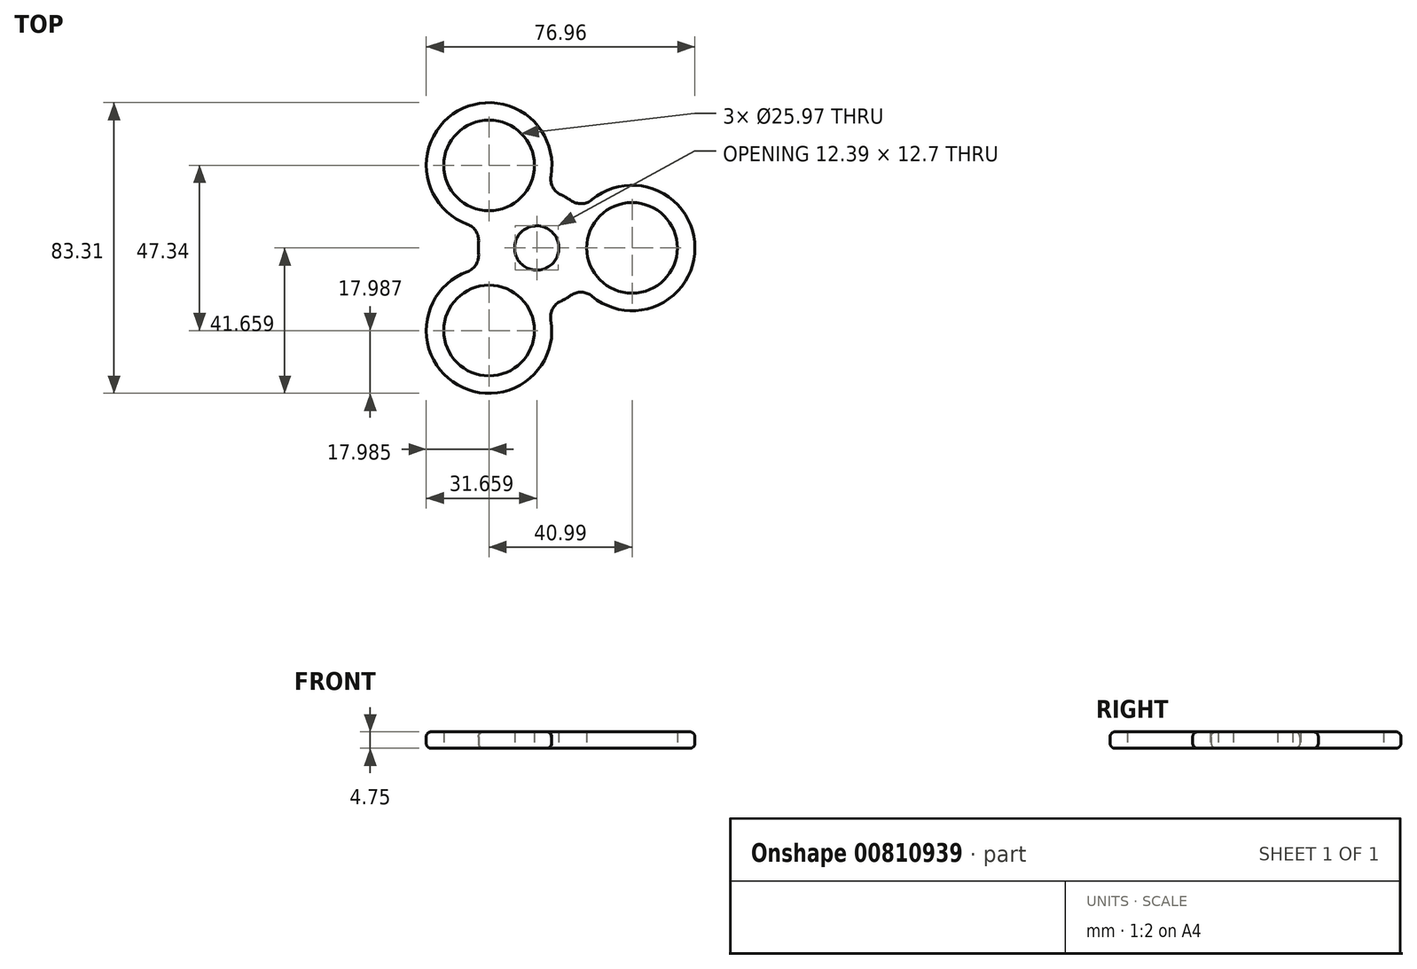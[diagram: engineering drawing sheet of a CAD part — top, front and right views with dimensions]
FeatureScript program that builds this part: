
annotation { "Feature Type Name" : "Feature", "Feature Type Description" : "" }
export const myFeature = defineFeature(function(context is Context, id is Id, definition is map)
    precondition{}
    {
        {
            var Q0;
            Q0=qCreatedBy(makeId("Top.planeOp"),FACE);
            var sketch = newSketch(context, id + "F0", { "sketchPlane" : qUnion([Q0])});
            skCircle(sketch, "E0", {"center": v(0, 0) * mm, "radius": 6.34 * mm});
            skCircle(sketch, "E1.1.4", {"center": v(0, 0.02) * mm, "radius": 6.33 * mm});
            skCircle(sketch, "E2", {"center": v(-13.68, -23.66) * mm, "radius": 12.98 * mm});
            skCircle(sketch, "E3", {"center": v(27.31, 0.02) * mm, "radius": 12.98 * mm});
            skCircle(sketch, "E4", {"center": v(-13.66, 23.68) * mm, "radius": 12.98 * mm});
            skArc(sketch, "E5.0", {"start": v(6.91, -15.23) * mm, "mid": v(8.36, -14.48) * mm, "end": v(9.73, -13.6) * mm});
            skArc(sketch, "E6.0", {"start": v(15.83, -13.82) * mm, "mid": v(45.3, 0.02) * mm, "end": v(15.83, 13.86) * mm});
            skArc(sketch, "E7.0", {"start": v(-19.9, -6.8) * mm, "mid": v(-22.67, -39.24) * mm, "end": v(4.05, -20.62) * mm});
            skArc(sketch, "E8.0", {"start": v(4.07, 20.65) * mm, "mid": v(-22.65, 39.25) * mm, "end": v(-19.9, 6.81) * mm});
            skArc(sketch, "E9.trimOffspring", {"start": v(9.73, 13.64) * mm, "mid": v(8.37, 14.52) * mm, "end": v(6.93, 15.26) * mm});
            skArc(sketch, "E10.trimOffspring", {"start": v(-16.66, 1.64) * mm, "mid": v(-16.74, 0.01) * mm, "end": v(-16.66, -1.61) * mm});
            skPoint(sketch, "E11.visualSharp", {"position": v(2.84, 16.52) * mm});
            skArc(sketch, "E11.filletArc", {"start": v(4.07, 20.65) * mm, "mid": v(4.58, 17.47) * mm, "end": v(6.93, 15.26) * mm});
            skPoint(sketch, "E12.visualSharp", {"position": v(12.87, 10.73) * mm});
            skArc(sketch, "E12.filletArc", {"start": v(9.73, 13.64) * mm, "mid": v(12.82, 12.71) * mm, "end": v(15.83, 13.86) * mm});
            skPoint(sketch, "E13.visualSharp", {"position": v(-15.7, -5.8) * mm});
            skArc(sketch, "E13.filletArc", {"start": v(-19.9, -6.8) * mm, "mid": v(-17.4, -4.76) * mm, "end": v(-16.66, -1.61) * mm});
            skPoint(sketch, "E14.visualSharp", {"position": v(-15.7, 5.8) * mm});
            skArc(sketch, "E14.filletArc", {"start": v(-16.66, 1.64) * mm, "mid": v(-17.4, 4.78) * mm, "end": v(-19.9, 6.81) * mm});
            skPoint(sketch, "E15.visualSharp", {"position": v(2.81, -16.48) * mm});
            skArc(sketch, "E15.filletArc", {"start": v(6.91, -15.23) * mm, "mid": v(4.56, -17.44) * mm, "end": v(4.05, -20.62) * mm});
            skPoint(sketch, "E16.visualSharp", {"position": v(12.87, -10.69) * mm});
            skArc(sketch, "E16.filletArc", {"start": v(15.83, -13.82) * mm, "mid": v(12.82, -12.67) * mm, "end": v(9.73, -13.6) * mm});
            skSolve(sketch);
        }
        {
            var Q0;
            Q0=makeQuery(id+"F0.imprint","IMPRINT",FACE,{"disambiguationData":[TD([[makeQuery(id+"F0.imprint","IMPRINT",EDGE,{"derivedFrom":sQuery(id+"F0.wireOp",EDGE,"E2")}),-1.0]])]});
            extrude(context, id + "F1", {"entities" : qUnion([Q0]), "depth" : 4.75 * mm, "offsetDistance" : 25 * mm});
        }
        {
            var Q0;
            Q0=makeQuery(id+"F1.opExtrude","CAP_EDGE",EDGE,{"disambiguationData":[OSD([sQuery(id+"F0.wireOp",EDGE,"E7.0")])],"isStart":false});
            var Q1;
            Q1=makeQuery(id+"F1.opExtrude","CAP_EDGE",EDGE,{"disambiguationData":[OSD([sQuery(id+"F0.wireOp",EDGE,"E6.0")])],"isStart":true});
            var Q2;
            Q2=makeQuery(id+"F1.opExtrude","CAP_EDGE",EDGE,{"disambiguationData":[OSD([sQuery(id+"F0.wireOp",EDGE,"E13.filletArc")])],"isStart":true});
            var Q3;
            Q3=makeQuery(id+"F1.opExtrude","CAP_EDGE",EDGE,{"disambiguationData":[OSD([sQuery(id+"F0.wireOp",EDGE,"E7.0")])],"isStart":true});
            var Q4;
            Q4=makeQuery(id+"F1.opExtrude","CAP_EDGE",EDGE,{"disambiguationData":[OSD([sQuery(id+"F0.wireOp",EDGE,"E10.trimOffspring")])],"isStart":true});
            var Q5;
            Q5=makeQuery(id+"F1.opExtrude","CAP_EDGE",EDGE,{"disambiguationData":[OSD([sQuery(id+"F0.wireOp",EDGE,"E14.filletArc")])],"isStart":true});
            var Q6;
            Q6=makeQuery(id+"F1.opExtrude","CAP_EDGE",EDGE,{"disambiguationData":[OSD([sQuery(id+"F0.wireOp",EDGE,"E8.0")])],"isStart":true});
            var Q7;
            Q7=makeQuery(id+"F1.opExtrude","CAP_EDGE",EDGE,{"disambiguationData":[OSD([sQuery(id+"F0.wireOp",EDGE,"E15.filletArc")])],"isStart":false});
            var Q8;
            Q8=makeQuery(id+"F1.opExtrude","CAP_EDGE",EDGE,{"disambiguationData":[OSD([sQuery(id+"F0.wireOp",EDGE,"E5.0")])],"isStart":false});
            var Q9;
            Q9=makeQuery(id+"F1.opExtrude","CAP_EDGE",EDGE,{"disambiguationData":[OSD([sQuery(id+"F0.wireOp",EDGE,"E16.filletArc")])],"isStart":false});
            var Q10;
            Q10=makeQuery(id+"F1.opExtrude","CAP_EDGE",EDGE,{"disambiguationData":[OSD([sQuery(id+"F0.wireOp",EDGE,"E16.filletArc")])],"isStart":true});
            var Q11;
            Q11=makeQuery(id+"F1.opExtrude","CAP_EDGE",EDGE,{"disambiguationData":[OSD([sQuery(id+"F0.wireOp",EDGE,"E5.0")])],"isStart":true});
            var Q12;
            Q12=makeQuery(id+"F1.opExtrude","CAP_EDGE",EDGE,{"disambiguationData":[OSD([sQuery(id+"F0.wireOp",EDGE,"E15.filletArc")])],"isStart":true});
            var Q13;
            Q13=makeQuery(id+"F1.opExtrude","CAP_EDGE",EDGE,{"disambiguationData":[OSD([sQuery(id+"F0.wireOp",EDGE,"E6.0")])],"isStart":false});
            var Q14;
            Q14=makeQuery(id+"F1.opExtrude","CAP_EDGE",EDGE,{"disambiguationData":[OSD([sQuery(id+"F0.wireOp",EDGE,"E12.filletArc")])],"isStart":false});
            var Q15;
            Q15=makeQuery(id+"F1.opExtrude","CAP_EDGE",EDGE,{"disambiguationData":[OSD([sQuery(id+"F0.wireOp",EDGE,"E9.trimOffspring")])],"isStart":false});
            var Q16;
            Q16=makeQuery(id+"F1.opExtrude","CAP_EDGE",EDGE,{"disambiguationData":[OSD([sQuery(id+"F0.wireOp",EDGE,"E8.0")])],"isStart":false});
            var Q17;
            Q17=makeQuery(id+"F1.opExtrude","CAP_EDGE",EDGE,{"disambiguationData":[OSD([sQuery(id+"F0.wireOp",EDGE,"E11.filletArc")])],"isStart":false});
            var Q18;
            Q18=makeQuery(id+"F1.opExtrude","CAP_EDGE",EDGE,{"disambiguationData":[OSD([sQuery(id+"F0.wireOp",EDGE,"E9.trimOffspring")])],"isStart":true});
            var Q19;
            Q19=makeQuery(id+"F1.opExtrude","CAP_EDGE",EDGE,{"disambiguationData":[OSD([sQuery(id+"F0.wireOp",EDGE,"E11.filletArc")])],"isStart":true});
            var Q20;
            Q20=makeQuery(id+"F1.opExtrude","CAP_EDGE",EDGE,{"disambiguationData":[OSD([sQuery(id+"F0.wireOp",EDGE,"E10.trimOffspring")])],"isStart":false});
            var Q21;
            Q21=makeQuery(id+"F1.opExtrude","CAP_EDGE",EDGE,{"disambiguationData":[OSD([sQuery(id+"F0.wireOp",EDGE,"E13.filletArc")])],"isStart":false});
            var Q22;
            Q22=makeQuery(id+"F1.opExtrude","CAP_EDGE",EDGE,{"disambiguationData":[OSD([sQuery(id+"F0.wireOp",EDGE,"E14.filletArc")])],"isStart":false});
            var Q23;
            Q23=makeQuery(id+"F1.opExtrude","CAP_EDGE",EDGE,{"disambiguationData":[OSD([sQuery(id+"F0.wireOp",EDGE,"E12.filletArc")])],"isStart":true});
            fillet(context, id + "F2", {"entities" : qUnion([Q0, Q1, Q2, Q3, Q4, Q5, Q6, Q7, Q8, Q9, Q10, Q11, Q12, Q13, Q14, Q15, Q16, Q17, Q18, Q19, Q20, Q21, Q22, Q23]), "radius" : 1.45 * mm, "tangentPropagation" : true, "allowEdgeOverflow" : false});
        }
    });
